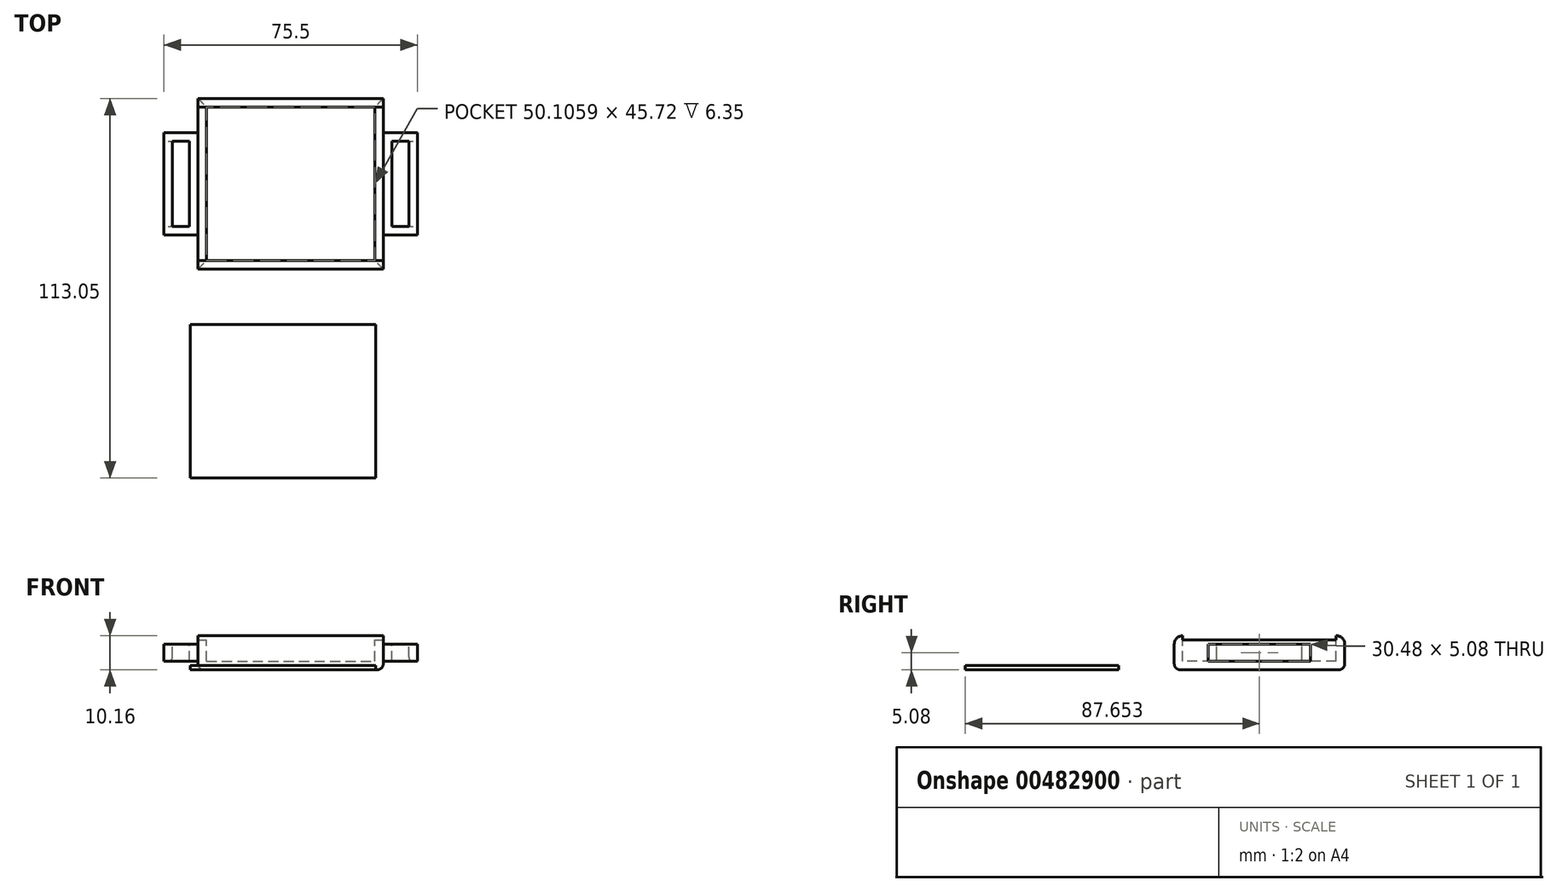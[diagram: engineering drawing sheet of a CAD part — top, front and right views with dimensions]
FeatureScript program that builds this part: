
annotation { "Feature Type Name" : "Feature", "Feature Type Description" : "" }
export const myFeature = defineFeature(function(context is Context, id is Id, definition is map)
    precondition{}
    {
        {
            var Q0;
            Q0=qCreatedBy(makeId("Top.planeOp"),FACE);
            var sketch = newSketch(context, id + "F0", { "sketchPlane" : qUnion([Q0])});
            skLineSegment(sketch, "E0.bottom", {"start": v(-26.35, 37.43) * mm, "end": v(28.83, 37.43) * mm});
            skLineSegment(sketch, "E0.top", {"start": v(-26.35, -13.37) * mm, "end": v(28.83, -13.37) * mm});
            skLineSegment(sketch, "E0.left", {"start": v(-26.35, 37.43) * mm, "end": v(-26.35, -13.37) * mm});
            skLineSegment(sketch, "E0.right", {"start": v(28.83, 37.43) * mm, "end": v(28.83, -13.37) * mm});
            skSolve(sketch);
        }
        {
            var Q0;
            Q0 = qSketchRegion(id + "F0", true);
            extrude(context, id + "F1", {"entities" : qUnion([Q0]), "depth" : 10.16 * mm});
        }
        {
            var Q0;
            Q0=makeQuery(id+"F1.opExtrude","SWEPT_FACE",FACE,{"disambiguationData":[OSD([sQuery(id+"F0.wireOp",EDGE,"E0.right")])]});
            var sketch = newSketch(context, id + "F2", { "sketchPlane" : qUnion([Q0])});
            skLineSegment(sketch, "E1.bottom", {"start": v(-3.2, 7.62) * mm, "end": v(27.27, 7.62) * mm});
            skLineSegment(sketch, "E1.top", {"start": v(-3.2, 2.54) * mm, "end": v(27.27, 2.54) * mm});
            skLineSegment(sketch, "E1.left", {"start": v(-3.2, 7.62) * mm, "end": v(-3.2, 2.54) * mm});
            skLineSegment(sketch, "E1.right", {"start": v(27.27, 7.62) * mm, "end": v(27.27, 2.54) * mm});
            skSolve(sketch);
        }
        {
            var Q0;
            Q0 = qSketchRegion(id + "F2", true);
            extrude(context, id + "F3", {"entities" : qUnion([Q0]), "operationType" : NewBodyOperationType.ADD, "depth" : 10.16 * mm});
        }
        {
            var Q0;
            Q0=makeQuery(id+"F1.opExtrude","SWEPT_FACE",FACE,{"disambiguationData":[OSD([sQuery(id+"F0.wireOp",EDGE,"E0.left")])]});
            var sketch = newSketch(context, id + "F4", { "sketchPlane" : qUnion([Q0])});
            skLineSegment(sketch, "E2.bottom", {"start": v(-27.27, 7.62) * mm, "end": v(3.2, 7.62) * mm});
            skLineSegment(sketch, "E2.top", {"start": v(-27.27, 2.54) * mm, "end": v(3.2, 2.54) * mm});
            skLineSegment(sketch, "E2.left", {"start": v(-27.27, 7.62) * mm, "end": v(-27.27, 2.54) * mm});
            skLineSegment(sketch, "E2.right", {"start": v(3.2, 7.62) * mm, "end": v(3.2, 2.54) * mm});
            skSolve(sketch);
        }
        {
            var Q0;
            Q0 = qSketchRegion(id + "F4", true);
            extrude(context, id + "F5", {"entities" : qUnion([Q0]), "operationType" : NewBodyOperationType.ADD, "depth" : 10.16 * mm});
        }
        {
            var Q0;
            Q0=makeQuery(id+"F1.opExtrude","CAP_FACE",FACE,{"disambiguationData":[OSD([sQuery(id+"F0.wireOp",EDGE,"E0.bottom"),sQuery(id+"F0.wireOp",EDGE,"E0.top"),sQuery(id+"F0.wireOp",EDGE,"E0.left"),sQuery(id+"F0.wireOp",EDGE,"E0.right")])],"isStart":false});
            var sketch = newSketch(context, id + "F6", { "sketchPlane" : qUnion([Q0])});
            skLineSegment(sketch, "E3.bottom", {"start": v(-23.81, 34.9) * mm, "end": v(26.3, 34.9) * mm});
            skLineSegment(sketch, "E3.top", {"start": v(-23.81, -10.83) * mm, "end": v(26.3, -10.83) * mm});
            skLineSegment(sketch, "E3.left", {"start": v(-23.81, 34.9) * mm, "end": v(-23.81, -10.83) * mm});
            skLineSegment(sketch, "E3.right", {"start": v(26.3, 34.9) * mm, "end": v(26.3, -10.83) * mm});
            skSolve(sketch);
        }
        {
            var Q0;
            Q0 = qSketchRegion(id + "F6", true);
            extrude(context, id + "F7", {"entities" : qUnion([Q0]), "operationType" : NewBodyOperationType.REMOVE, "oppositeDirection" : true, "depth" : 7.62 * mm});
        }
        {
            var Q0;
            Q0=makeQuery(id+"F1.opExtrude","CAP_EDGE",EDGE,{"disambiguationData":[OSD([sQuery(id+"F0.wireOp",EDGE,"E0.top")])],"isStart":false});
            var Q1;
            Q1=makeQuery(id+"F1.opExtrude","CAP_EDGE",EDGE,{"disambiguationData":[OSD([sQuery(id+"F0.wireOp",EDGE,"E0.bottom")])],"isStart":false});
            fillet(context, id + "F8", {"entities" : qUnion([Q0, Q1]), "radius" : 2.54 * mm, "tangentPropagation" : true, "allowEdgeOverflow" : false});
        }
        {
            var Q0;
            Q0=makeQuery(id+"F8.opFillet","SPLIT",FACE,{"disambiguationData":[OD(1.0)],"derivedFrom":makeQuery(id+"F1.opExtrude","CAP_FACE",FACE,{"disambiguationData":[OSD([sQuery(id+"F0.wireOp",EDGE,"E0.bottom"),sQuery(id+"F0.wireOp",EDGE,"E0.top"),sQuery(id+"F0.wireOp",EDGE,"E0.left"),sQuery(id+"F0.wireOp",EDGE,"E0.right")])],"isStart":false})});
            var sketch = newSketch(context, id + "F9", { "sketchPlane" : qUnion([Q0])});
            skLineSegment(sketch, "E4.bottom", {"start": v(28.83, 34.9) * mm, "end": v(26.3, 34.9) * mm});
            skLineSegment(sketch, "E4.top", {"start": v(28.83, -10.83) * mm, "end": v(26.3, -10.83) * mm});
            skLineSegment(sketch, "E4.left", {"start": v(28.83, 34.9) * mm, "end": v(28.83, -10.83) * mm});
            skLineSegment(sketch, "E4.right", {"start": v(26.3, 34.9) * mm, "end": v(26.3, -10.83) * mm});
            skLineSegment(sketch, "E5.bottom", {"start": v(-26.35, 34.9) * mm, "end": v(-23.81, 34.9) * mm});
            skLineSegment(sketch, "E5.top", {"start": v(-26.35, -10.83) * mm, "end": v(-23.81, -10.83) * mm});
            skLineSegment(sketch, "E5.left", {"start": v(-26.35, 34.9) * mm, "end": v(-26.35, -10.83) * mm});
            skLineSegment(sketch, "E5.right", {"start": v(-23.81, 34.9) * mm, "end": v(-23.81, -10.83) * mm});
            skSolve(sketch);
        }
        {
            var Q0;
            Q0 = qSketchRegion(id + "F9", true);
            extrude(context, id + "F10", {"entities" : qUnion([Q0]), "operationType" : NewBodyOperationType.REMOVE, "oppositeDirection" : true, "depth" : 1.27 * mm});
        }
        {
            var Q0;
            Q0=qCreatedBy(makeId("Top.planeOp"),FACE);
            var sketch = newSketch(context, id + "F11", { "sketchPlane" : qUnion([Q0])});
            skLineSegment(sketch, "E6.bottom", {"start": v(-28.64, -29.9) * mm, "end": v(26.55, -29.9) * mm});
            skLineSegment(sketch, "E6.top", {"start": v(-28.64, -75.62) * mm, "end": v(26.55, -75.62) * mm});
            skLineSegment(sketch, "E6.left", {"start": v(-28.64, -29.9) * mm, "end": v(-28.64, -75.62) * mm});
            skLineSegment(sketch, "E6.right", {"start": v(26.55, -29.9) * mm, "end": v(26.55, -75.62) * mm});
            skSolve(sketch);
        }
        {
            var Q0;
            Q0 = qSketchRegion(id + "F11", true);
            extrude(context, id + "F12", {"entities" : qUnion([Q0]), "depth" : 1.27 * mm});
        }
        {
            var Q0;
            Q0=makeQuery(id+"F5.opExtrude","SWEPT_FACE",FACE,{"disambiguationData":[OSD([sQuery(id+"F4.wireOp",EDGE,"E2.bottom")])]});
            var sketch = newSketch(context, id + "F13", { "sketchPlane" : qUnion([Q0])});
            skLineSegment(sketch, "E7.bottom", {"start": v(-33.97, 24.73) * mm, "end": v(-28.9, 24.73) * mm});
            skLineSegment(sketch, "E7.top", {"start": v(-33.97, -0.67) * mm, "end": v(-28.9, -0.67) * mm});
            skLineSegment(sketch, "E7.left", {"start": v(-33.97, 24.73) * mm, "end": v(-33.97, -0.67) * mm});
            skLineSegment(sketch, "E7.right", {"start": v(-28.9, 24.73) * mm, "end": v(-28.9, -0.67) * mm});
            skLineSegment(sketch, "E8.bottom", {"start": v(31.37, 24.73) * mm, "end": v(36.45, 24.73) * mm});
            skLineSegment(sketch, "E8.top", {"start": v(31.37, -0.67) * mm, "end": v(36.45, -0.67) * mm});
            skLineSegment(sketch, "E8.left", {"start": v(31.37, 24.73) * mm, "end": v(31.37, -0.67) * mm});
            skLineSegment(sketch, "E8.right", {"start": v(36.45, 24.73) * mm, "end": v(36.45, -0.67) * mm});
            skSolve(sketch);
        }
        {
            var Q0;
            Q0 = qSketchRegion(id + "F13", true);
            extrude(context, id + "F14", {"entities" : qUnion([Q0]), "operationType" : NewBodyOperationType.REMOVE, "oppositeDirection" : true, "depth" : 25.4 * mm});
        }
        {
            var Q0;
            Q0=makeQuery(id+"F14.boolean.opBoolean","COPY",EDGE,{"derivedFrom":makeQuery(id+"F14.opExtrude","CAP_EDGE",EDGE,{"disambiguationData":[OSD([sQuery(id+"F13.wireOp",EDGE,"E7.left")])],"isStart":true})});
            var Q1;
            Q1=makeQuery(id+"F14.boolean.opBoolean","INTERSECT",EDGE,{"derivedFrom":[makeQuery(id+"F5.opExtrude","SWEPT_FACE",FACE,{"disambiguationData":[OSD([sQuery(id+"F4.wireOp",EDGE,"E2.top")])]}),makeQuery(id+"F14.opExtrude","SWEPT_FACE",FACE,{"disambiguationData":[OSD([sQuery(id+"F13.wireOp",EDGE,"E7.left")])]})]});
            var Q2;
            Q2=makeQuery(id+"F14.boolean.opBoolean","INTERSECT",EDGE,{"derivedFrom":[makeQuery(id+"F3.opExtrude","SWEPT_FACE",FACE,{"disambiguationData":[OSD([sQuery(id+"F2.wireOp",EDGE,"E1.top")])]}),makeQuery(id+"F14.opExtrude","SWEPT_FACE",FACE,{"disambiguationData":[OSD([sQuery(id+"F13.wireOp",EDGE,"E8.right")])]})]});
            var Q3;
            Q3=makeQuery(id+"F14.boolean.opBoolean","COPY",EDGE,{"derivedFrom":makeQuery(id+"F14.opExtrude","CAP_EDGE",EDGE,{"disambiguationData":[OSD([sQuery(id+"F13.wireOp",EDGE,"E8.right")])],"isStart":true})});
            fillet(context, id + "F15", {"entities" : qUnion([Q0, Q1, Q2, Q3]), "radius" : 1.27 * mm, "tangentPropagation" : true, "allowEdgeOverflow" : false});
        }
        {
            var Q0;
            Q0=makeQuery(id+"F1.opExtrude","CAP_EDGE",EDGE,{"disambiguationData":[OSD([sQuery(id+"F0.wireOp",EDGE,"E0.right")])],"isStart":true});
            var Q1;
            Q1=makeQuery(id+"F1.opExtrude","CAP_EDGE",EDGE,{"disambiguationData":[OSD([sQuery(id+"F0.wireOp",EDGE,"E0.bottom")])],"isStart":true});
            var Q2;
            Q2=makeQuery(id+"F1.opExtrude","CAP_EDGE",EDGE,{"disambiguationData":[OSD([sQuery(id+"F0.wireOp",EDGE,"E0.left")])],"isStart":true});
            var Q3;
            Q3=makeQuery(id+"F1.opExtrude","CAP_EDGE",EDGE,{"disambiguationData":[OSD([sQuery(id+"F0.wireOp",EDGE,"E0.top")])],"isStart":true});
            fillet(context, id + "F16", {"entities" : qUnion([Q0, Q1, Q2, Q3]), "radius" : 1.78 * mm, "tangentPropagation" : true, "allowEdgeOverflow" : false});
        }
    });
